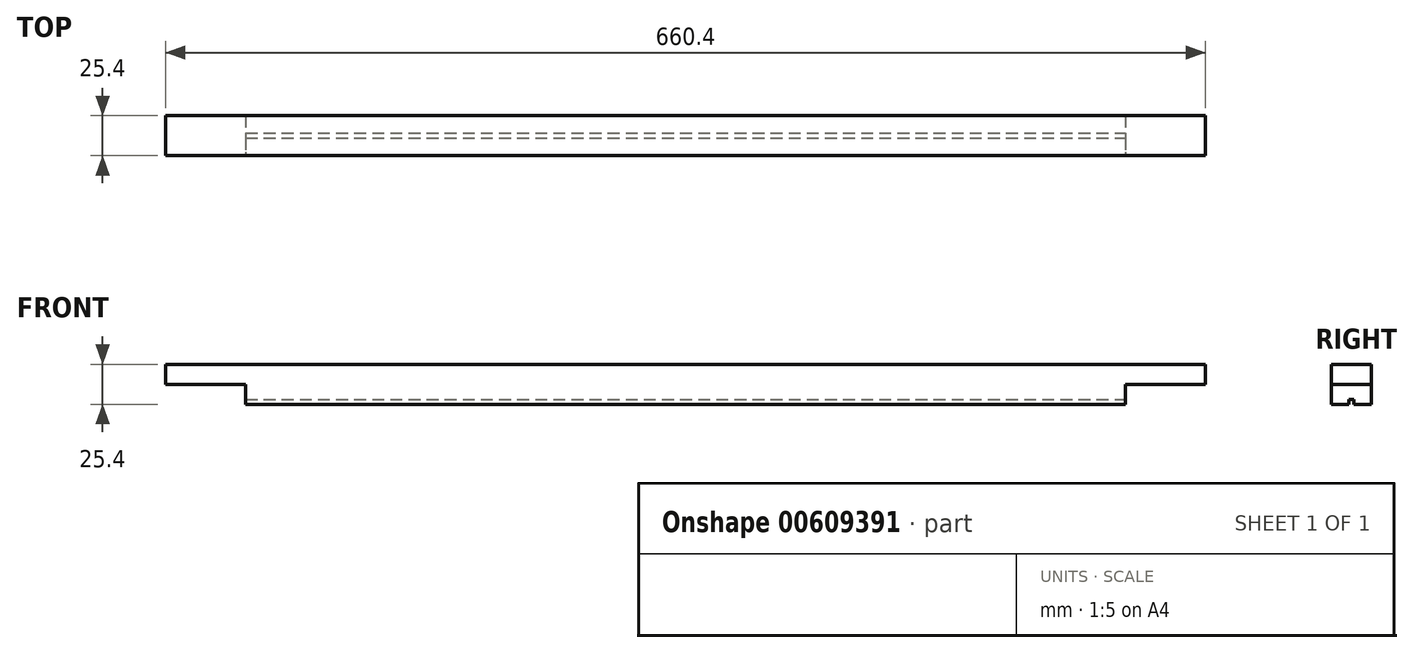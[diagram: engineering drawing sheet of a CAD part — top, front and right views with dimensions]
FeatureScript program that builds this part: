
annotation { "Feature Type Name" : "Feature", "Feature Type Description" : "" }
export const myFeature = defineFeature(function(context is Context, id is Id, definition is map)
    precondition{}
    {
        {
            var Q0;
            Q0=qCreatedBy(makeId("Front.planeOp"),FACE);
            var sketch = newSketch(context, id + "F0", { "sketchPlane" : qUnion([Q0])});
            skLineSegment(sketch, "E0.bottom", {"start": v(-330.2, 12.7) * mm, "end": v(330.2, 12.7) * mm});
            skLineSegment(sketch, "E0.top", {"start": v(-330.2, -12.7) * mm, "end": v(330.2, -12.7) * mm});
            skLineSegment(sketch, "E0.left", {"start": v(-330.2, 12.7) * mm, "end": v(-330.2, -12.7) * mm});
            skLineSegment(sketch, "E0.right", {"start": v(330.2, 12.7) * mm, "end": v(330.2, -12.7) * mm});
            skPoint(sketch, "E0.middle", {"position": v(0, 0) * mm});
            skSolve(sketch);
        }
        {
            var Q0;
            Q0=makeQuery(id+"F0.imprint","IMPRINT",FACE,{"disambiguationData":[TD([[makeQuery(id+"F0.imprint","IMPRINT",EDGE,{"derivedFrom":sQuery(id+"F0.wireOp",EDGE,"E0.bottom")}),-1.0]])]});
            extrude(context, id + "F1", {"entities" : qUnion([Q0]), "depth" : 25.4 * mm, "offsetDistance" : 25.4 * mm});
        }
        {
            var Q0;
            Q0=makeQuery(id+"F1.opExtrude","CAP_FACE",FACE,{"disambiguationData":[OSD([sQuery(id+"F0.wireOp",EDGE,"E0.bottom"),sQuery(id+"F0.wireOp",EDGE,"E0.top"),sQuery(id+"F0.wireOp",EDGE,"E0.left"),sQuery(id+"F0.wireOp",EDGE,"E0.right")])],"isStart":false});
            var sketch = newSketch(context, id + "F2", { "sketchPlane" : qUnion([Q0])});
            skLineSegment(sketch, "E1.bottom", {"start": v(-330.2, -12.7) * mm, "end": v(-279.4, -12.7) * mm});
            skLineSegment(sketch, "E1.top", {"start": v(-330.2, 0) * mm, "end": v(-279.4, 0) * mm});
            skLineSegment(sketch, "E1.left", {"start": v(-330.2, -12.7) * mm, "end": v(-330.2, 0) * mm});
            skLineSegment(sketch, "E1.right", {"start": v(-279.4, -12.7) * mm, "end": v(-279.4, 0) * mm});
            skLineSegment(sketch, "E2.bottom", {"start": v(330.2, -12.7) * mm, "end": v(279.4, -12.7) * mm});
            skLineSegment(sketch, "E2.top", {"start": v(330.2, 0) * mm, "end": v(279.4, 0) * mm});
            skLineSegment(sketch, "E2.left", {"start": v(330.2, -12.7) * mm, "end": v(330.2, 0) * mm});
            skLineSegment(sketch, "E2.right", {"start": v(279.4, -12.7) * mm, "end": v(279.4, 0) * mm});
            skSolve(sketch);
        }
        {
            var Q0;
            Q0=makeQuery(id+"F2.imprint","IMPRINT",FACE,{"disambiguationData":[TD([[makeQuery(id+"F2.imprint","IMPRINT",EDGE,{"derivedFrom":sQuery(id+"F2.wireOp",EDGE,"E1.bottom")}),1.0]])]});
            var Q1;
            Q1=makeQuery(id+"F2.imprint","IMPRINT",FACE,{"disambiguationData":[TD([[makeQuery(id+"F2.imprint","IMPRINT",EDGE,{"derivedFrom":sQuery(id+"F2.wireOp",EDGE,"E2.bottom")}),1.0]])]});
            extrude(context, id + "F3", {"entities" : qUnion([Q0, Q1]), "operationType" : NewBodyOperationType.REMOVE, "oppositeDirection" : true, "depth" : 25.4 * mm, "offsetDistance" : 25.4 * mm});
        }
        {
            var Q0;
            Q0=makeQuery(id+"F1.opExtrude","SWEPT_FACE",FACE,{"disambiguationData":[OSD([sQuery(id+"F0.wireOp",EDGE,"E0.top")])]});
            var sketch = newSketch(context, id + "F4", { "sketchPlane" : qUnion([Q0])});
            skLineSegment(sketch, "E3.bottom", {"start": v(-279.4, 14.29) * mm, "end": v(279.4, 14.29) * mm});
            skLineSegment(sketch, "E3.top", {"start": v(-279.4, 11.11) * mm, "end": v(279.4, 11.11) * mm});
            skLineSegment(sketch, "E3.left", {"start": v(-279.4, 14.29) * mm, "end": v(-279.4, 11.11) * mm});
            skLineSegment(sketch, "E3.right", {"start": v(279.4, 14.29) * mm, "end": v(279.4, 11.11) * mm});
            skPoint(sketch, "E3.middle", {"position": v(0, 12.7) * mm});
            skSolve(sketch);
        }
        {
            var Q0;
            Q0=makeQuery(id+"F4.imprint","IMPRINT",FACE,{"disambiguationData":[TD([[makeQuery(id+"F4.imprint","IMPRINT",EDGE,{"derivedFrom":sQuery(id+"F4.wireOp",EDGE,"E3.bottom")}),-1.0]])]});
            extrude(context, id + "F5", {"entities" : qUnion([Q0]), "operationType" : NewBodyOperationType.REMOVE, "oppositeDirection" : true, "depth" : 3.17 * mm, "offsetDistance" : 25.4 * mm});
        }
    });
